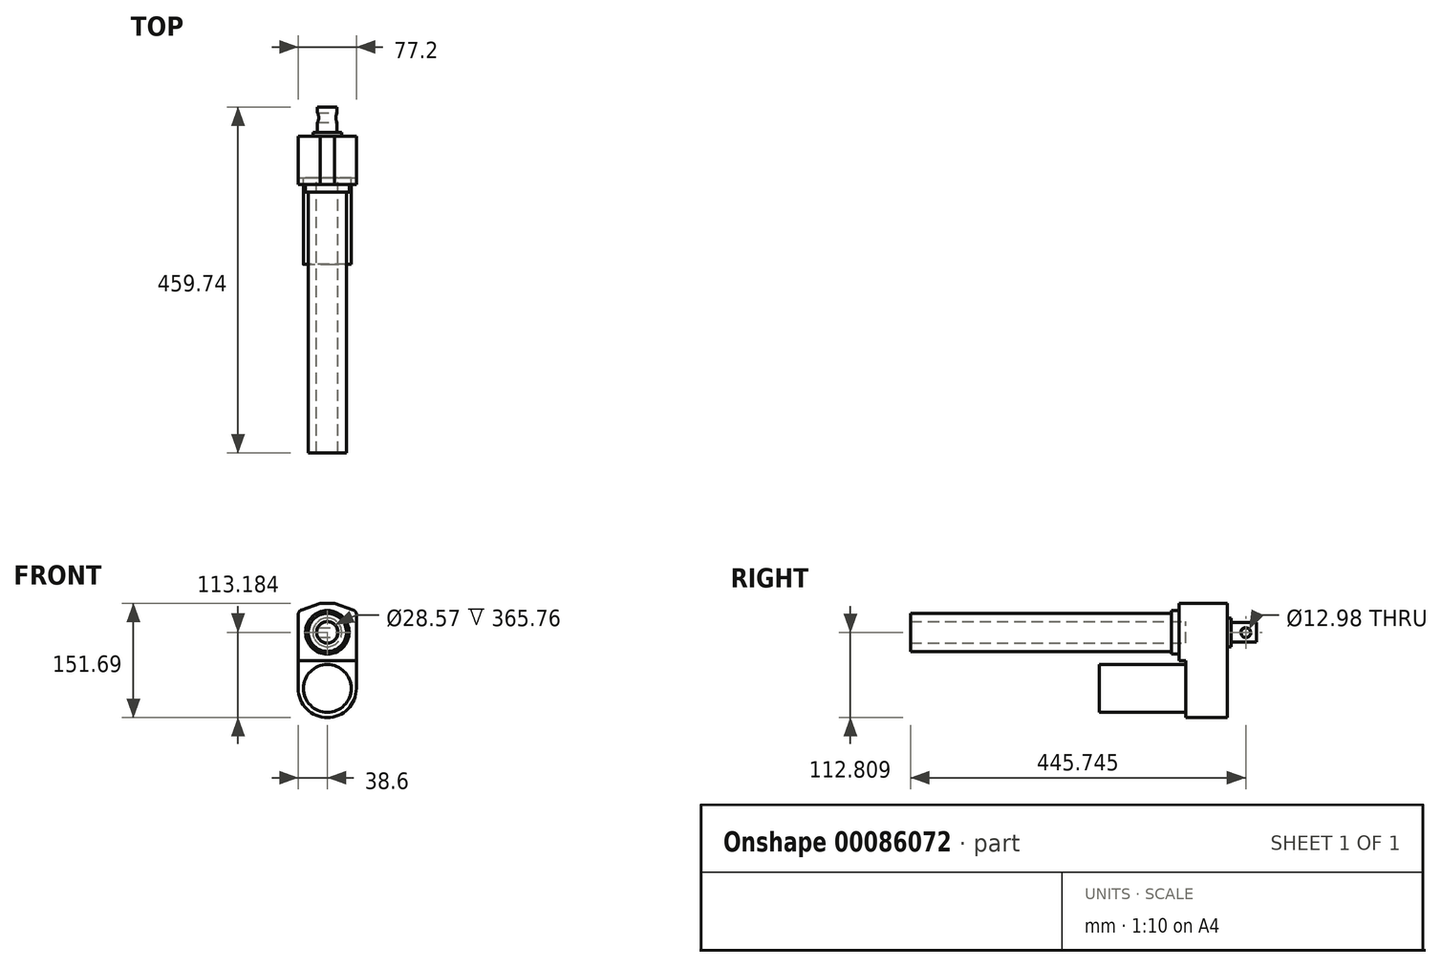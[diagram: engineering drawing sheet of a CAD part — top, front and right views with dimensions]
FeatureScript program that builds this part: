
annotation { "Feature Type Name" : "Feature", "Feature Type Description" : "" }
export const myFeature = defineFeature(function(context is Context, id is Id, definition is map)
    precondition{}
    {
        {
            var Q0;
            Q0=qCreatedBy(makeId("Front.planeOp"),FACE);
            var sketch = newSketch(context, id + "F0", { "sketchPlane" : qUnion([Q0])});
            skLineSegment(sketch, "E0", {"start": v(-38.6, 42.06) * mm, "end": v(-38.6, -56.39) * mm});
            skLineSegment(sketch, "E1", {"start": v(38.6, 42.06) * mm, "end": v(38.6, -56.39) * mm});
            skLineSegment(sketch, "E2", {"start": v(-38.6, 46.57) * mm, "end": v(38.6, 46.57) * mm, "construction": true});
            skLineSegment(sketch, "E3", {"start": v(-38.6, -56.39) * mm, "end": v(38.6, -56.39) * mm, "construction": true});
            skLineSegment(sketch, "E4", {"start": v(-9.57, 56.7) * mm, "end": v(9.48, 56.7) * mm});
            skLineSegment(sketch, "E5", {"start": v(9.48, 56.7) * mm, "end": v(34.33, 48.06) * mm});
            skLineSegment(sketch, "E6", {"start": v(-9.57, 56.7) * mm, "end": v(-34.34, 48.06) * mm});
            skArc(sketch, "E7", {"start": v(-38.6, -56.39) * mm, "mid": v(0, -94.99) * mm, "end": v(38.6, -56.39) * mm});
            skCircle(sketch, "E8", {"center": v(0, -56.39) * mm, "radius": 31.75 * mm});
            skLineSegment(sketch, "E9", {"start": v(-38.6, -19.31) * mm, "end": v(38.6, -19.31) * mm});
            skCircle(sketch, "E10", {"center": v(0, 18.2) * mm, "radius": 28.95 * mm});
            skCircle(sketch, "E11", {"center": v(0, 18.2) * mm, "radius": 25.33 * mm});
            skCircle(sketch, "E12", {"center": v(0, 18.2) * mm, "radius": 14.29 * mm});
            skPoint(sketch, "E13.visualSharp", {"position": v(-38.6, 46.57) * mm});
            skArc(sketch, "E13.filletArc", {"start": v(-34.34, 48.06) * mm, "mid": v(-37.42, 45.74) * mm, "end": v(-38.6, 42.06) * mm});
            skPoint(sketch, "E14.visualSharp", {"position": v(38.6, 46.57) * mm});
            skArc(sketch, "E14.filletArc", {"start": v(38.6, 42.06) * mm, "mid": v(37.42, 45.74) * mm, "end": v(34.33, 48.06) * mm});
            skSolve(sketch);
        }
        {
            var Q0;
            Q0=makeQuery(id+"F0.imprint","IMPRINT",FACE,{"disambiguationData":[TD([[makeQuery(id+"F0.imprint","IMPRINT",EDGE,{"derivedFrom":sQuery(id+"F0.wireOp",EDGE,"E12")}),1.0]])]});
            var Q1;
            Q1=makeQuery(id+"F0.imprint","IMPRINT",FACE,{"disambiguationData":[TD([[makeQuery(id+"F0.imprint","IMPRINT",EDGE,{"derivedFrom":sQuery(id+"F0.wireOp",EDGE,"E11")}),1.0]])]});
            var Q2;
            Q2=makeQuery(id+"F0.imprint","IMPRINT",FACE,{"disambiguationData":[TD([[makeQuery(id+"F0.imprint","IMPRINT",EDGE,{"derivedFrom":sQuery(id+"F0.wireOp",EDGE,"E10")}),1.0]])]});
            var Q3;
            Q3=makeQuery(id+"F0.imprint","IMPRINT",FACE,{"disambiguationData":[TD([[makeQuery(id+"F0.imprint","IMPRINT",EDGE,{"derivedFrom":sQuery(id+"F0.wireOp",EDGE,"E4")}),-1.0]])]});
            var Q4;
            {var subQ0=sQuery(id+"F0.wireOp",EDGE,"E7");Q4=makeQuery(id+"F0.imprint","IMPRINT",FACE,{"disambiguationData":[TD([[makeQuery(id+"F0.imprint","IMPRINT",EDGE,{"derivedFrom":subQ0}),1.0]])]});}
            var Q5;
            Q5=makeQuery(id+"F0.imprint","IMPRINT",FACE,{"disambiguationData":[TD([[makeQuery(id+"F0.imprint","IMPRINT",EDGE,{"derivedFrom":sQuery(id+"F0.wireOp",EDGE,"E8")}),1.0]])]});
            extrude(context, id + "F1", {"entities" : qUnion([Q0, Q1, Q2, Q3, Q4, Q5]), "oppositeDirection" : true, "depth" : 55.5 * mm});
        }
        {
            var Q0;
            Q0=makeQuery(id+"F0.imprint","IMPRINT",FACE,{"disambiguationData":[TD([[makeQuery(id+"F0.imprint","IMPRINT",EDGE,{"derivedFrom":sQuery(id+"F0.wireOp",EDGE,"E8")}),1.0]])]});
            extrude(context, id + "F2", {"entities" : qUnion([Q0]), "operationType" : NewBodyOperationType.ADD, "depth" : 114.99 * mm});
        }
        {
            var Q0;
            Q0=makeQuery(id+"F0.imprint","IMPRINT",FACE,{"disambiguationData":[TD([[makeQuery(id+"F0.imprint","IMPRINT",EDGE,{"derivedFrom":sQuery(id+"F0.wireOp",EDGE,"E11")}),1.0]])]});
            extrude(context, id + "F3", {"entities" : qUnion([Q0]), "operationType" : NewBodyOperationType.ADD, "depth" : 365.76 * mm});
        }
        {
            var Q0;
            Q0=makeQuery(id+"F0.imprint","IMPRINT",FACE,{"disambiguationData":[TD([[makeQuery(id+"F0.imprint","IMPRINT",EDGE,{"derivedFrom":sQuery(id+"F0.wireOp",EDGE,"E4")}),-1.0]])]});
            var Q1;
            Q1=sQuery(id+"F0.wireOp",EDGE,"E10");
            extrude(context, id + "F4", {"entities" : qUnion([Q0]), "operationType" : NewBodyOperationType.ADD, "surfaceEntities" : qUnion([Q1]), "depth" : 8.79 * mm});
        }
        {
            var Q0;
            Q0=makeQuery(id+"F0.imprint","IMPRINT",FACE,{"disambiguationData":[TD([[makeQuery(id+"F0.imprint","IMPRINT",EDGE,{"derivedFrom":sQuery(id+"F0.wireOp",EDGE,"E10")}),1.0]])]});
            extrude(context, id + "F5", {"entities" : qUnion([Q0]), "operationType" : NewBodyOperationType.ADD, "depth" : 19.05 * mm});
        }
        {
            var Q0;
            Q0=makeQuery(id+"F1.opExtrude","CAP_FACE",FACE,{"disambiguationData":[OSD([sQuery(id+"F0.wireOp",EDGE,"E0"),sQuery(id+"F0.wireOp",EDGE,"E1"),sQuery(id+"F0.wireOp",EDGE,"E4"),sQuery(id+"F0.wireOp",EDGE,"E5"),sQuery(id+"F0.wireOp",EDGE,"E6"),sQuery(id+"F0.wireOp",EDGE,"E7"),sQuery(id+"F0.wireOp",EDGE,"E13.filletArc"),sQuery(id+"F0.wireOp",EDGE,"E14.filletArc")])],"isStart":false});
            var sketch = newSketch(context, id + "F6", { "sketchPlane" : qUnion([Q0])});
            skCircle(sketch, "E15", {"center": v(0, 18.11) * mm, "radius": 19.07 * mm});
            skCircle(sketch, "E16", {"center": v(0, 18.11) * mm, "radius": 13 * mm});
            skLineSegment(sketch, "E17", {"start": v(0, 18.11) * mm, "end": v(0, 18.11) * mm});
            skSolve(sketch);
        }
        {
            var Q0;
            Q0=makeQuery(id+"F6.imprint","IMPRINT",FACE,{"disambiguationData":[TD([[makeQuery(id+"F6.imprint","IMPRINT",EDGE,{"derivedFrom":sQuery(id+"F6.wireOp",EDGE,"E16")}),1.0]])]});
            extrude(context, id + "F7", {"entities" : qUnion([Q0]), "operationType" : NewBodyOperationType.ADD, "depth" : 38.48 * mm});
        }
        {
            var Q0;
            Q0=makeQuery(id+"F6.imprint","IMPRINT",FACE,{"disambiguationData":[TD([[makeQuery(id+"F6.imprint","IMPRINT",EDGE,{"derivedFrom":sQuery(id+"F6.wireOp",EDGE,"E15")}),1.0]])]});
            extrude(context, id + "F8", {"entities" : qUnion([Q0]), "operationType" : NewBodyOperationType.ADD, "depth" : 5.08 * mm});
        }
        {
            var Q0;
            Q0=qCreatedBy(makeId("Right.planeOp"),FACE);
            var sketch = newSketch(context, id + "F9", { "sketchPlane" : qUnion([Q0])});
            skCircle(sketch, "E18", {"center": v(79.98, 17.82) * mm, "radius": 6.49 * mm});
            skSolve(sketch);
        }
        {
            var Q0;
            Q0 = qSketchRegion(id + "F9", true);
            var Q1;
            Q1=sQuery(id+"F9.wireOp",EDGE,"E18");
            extrude(context, id + "F10", {"entities" : qUnion([Q0]), "operationType" : NewBodyOperationType.REMOVE, "surfaceEntities" : qUnion([Q1]), "oppositeDirection" : true, "depth" : 25.4 * mm});
        }
        {
            var Q0;
            Q0 = qSketchRegion(id + "F9", true);
            extrude(context, id + "F11", {"entities" : qUnion([Q0]), "operationType" : NewBodyOperationType.REMOVE, "endBound" : BoundingType.SYMMETRIC, "oppositeDirection" : true, "depth" : 50.8 * mm});
        }
    });
